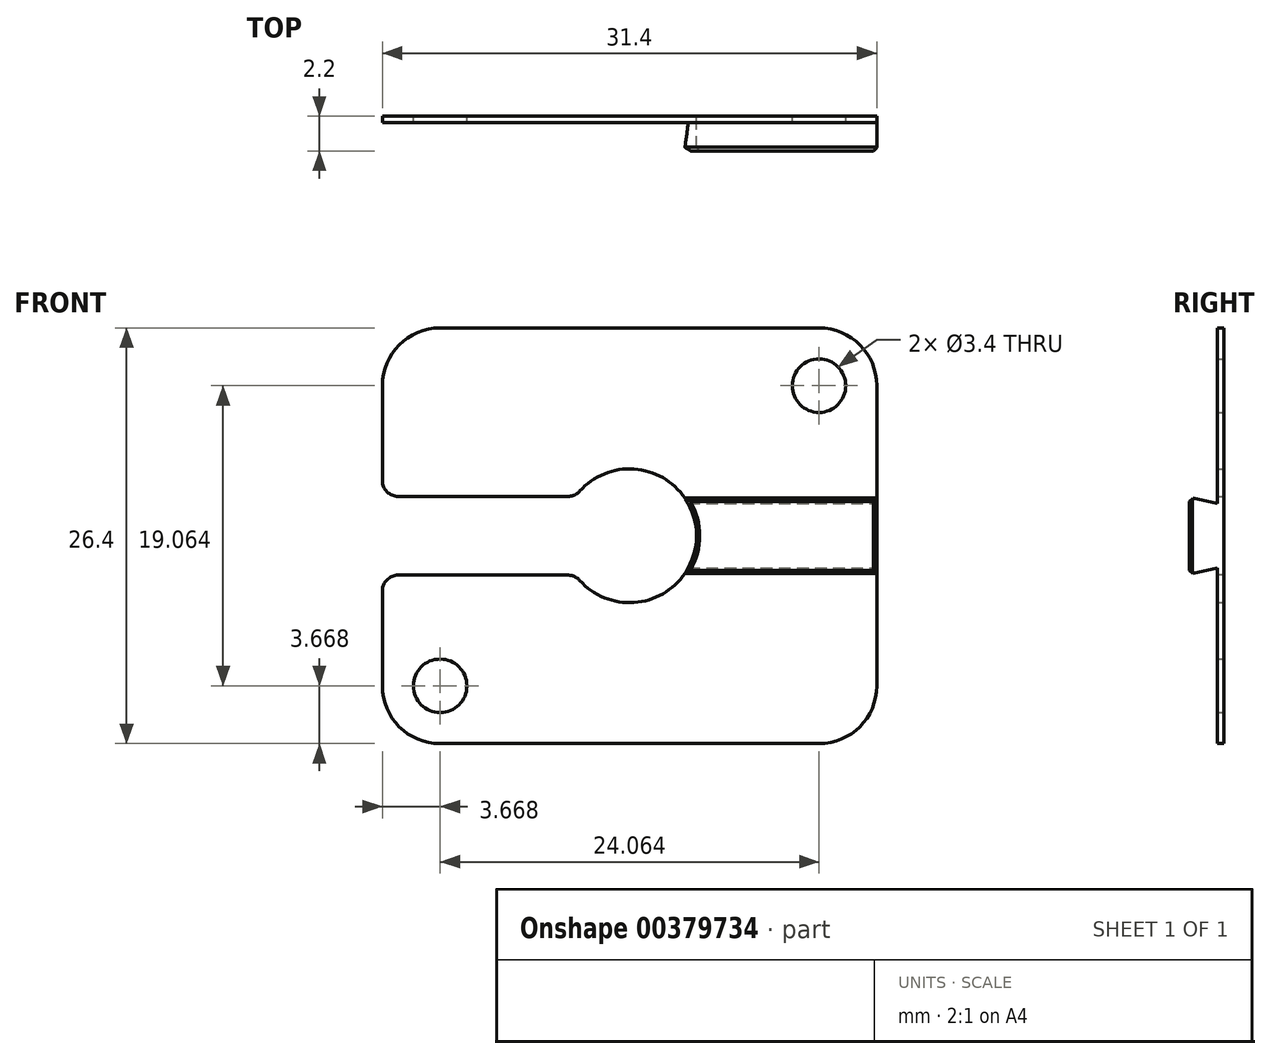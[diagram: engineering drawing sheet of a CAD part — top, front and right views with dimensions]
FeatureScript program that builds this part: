
annotation { "Feature Type Name" : "Feature", "Feature Type Description" : "" }
export const myFeature = defineFeature(function(context is Context, id is Id, definition is map)
    precondition{}
    {
        {
            var Q0;
            Q0=qCreatedBy(makeId("Front.planeOp"),FACE);
            var sketch = newSketch(context, id + "F0", { "sketchPlane" : qUnion([Q0])});
            skLineSegment(sketch, "E0.bottom", {"start": v(-15.7, 13.2) * mm, "end": v(15.7, 13.2) * mm});
            skLineSegment(sketch, "E0.top", {"start": v(-15.7, -13.2) * mm, "end": v(15.7, -13.2) * mm});
            skLineSegment(sketch, "E0.left", {"start": v(-15.7, 13.2) * mm, "end": v(-15.7, -13.2) * mm});
            skLineSegment(sketch, "E0.right", {"start": v(15.7, 13.2) * mm, "end": v(15.7, -13.2) * mm});
            skLineSegment(sketch, "E1.right", {"start": v(0, 0) * mm, "end": v(0, 13.2) * mm, "construction": true});
            skLineSegment(sketch, "E2.bottom", {"start": v(0, 0) * mm, "end": v(-15.7, 0) * mm, "construction": true});
            skLineSegment(sketch, "E2.top", {"start": v(0, 0) * mm, "end": v(-15.7, 0) * mm, "construction": true});
            skLineSegment(sketch, "E2.left", {"start": v(0, 0) * mm, "end": v(0, 0) * mm});
            skLineSegment(sketch, "E2.right", {"start": v(-15.7, 0) * mm, "end": v(-15.7, 0) * mm});
            skLineSegment(sketch, "E3", {"start": v(-12.03, 9.53) * mm, "end": v(12.03, -9.53) * mm, "construction": true});
            skCircle(sketch, "E4", {"center": v(-12.03, 9.53) * mm, "radius": 1.7 * mm, "construction": true});
            skCircle(sketch, "E5", {"center": v(12.03, -9.53) * mm, "radius": 1.7 * mm, "construction": true});
            skCircle(sketch, "E6", {"center": v(-12.03, 9.53) * mm, "radius": 3.67 * mm, "construction": true});
            skCircle(sketch, "E7", {"center": v(12.03, -9.53) * mm, "radius": 3.67 * mm, "construction": true});
            skCircle(sketch, "E8.MirrorC", {"center": v(12.03, 9.53) * mm, "radius": 1.7 * mm});
            skCircle(sketch, "E9.MirrorC", {"center": v(-12.03, -9.53) * mm, "radius": 1.7 * mm});
            skSolve(sketch);
        }
        {
            var Q0;
            Q0=qSketchRegion(id+"F0",true);
            extrude(context, id + "F1", {"entities" : qUnion([Q0]), "depth" : 0.4 * mm, "offsetDistance" : 25 * mm});
        }
        {
            var Q0;
            Q0=makeQuery(id+"F1.opExtrude","SWEPT_EDGE",EDGE,{"disambiguationData":[OSD([sQuery(id+"F0.wireOp",EDGE,"E0.top"),sQuery(id+"F0.wireOp",EDGE,"E0.right")])]});
            var Q1;
            Q1=makeQuery(id+"F1.opExtrude","SWEPT_EDGE",EDGE,{"disambiguationData":[OSD([sQuery(id+"F0.wireOp",EDGE,"E0.bottom"),sQuery(id+"F0.wireOp",EDGE,"E0.right")])]});
            var Q2;
            Q2=makeQuery(id+"F1.opExtrude","SWEPT_EDGE",EDGE,{"disambiguationData":[OSD([sQuery(id+"F0.wireOp",EDGE,"E0.top"),sQuery(id+"F0.wireOp",EDGE,"E0.left")])]});
            var Q3;
            Q3=makeQuery(id+"F1.opExtrude","SWEPT_EDGE",EDGE,{"disambiguationData":[OSD([sQuery(id+"F0.wireOp",EDGE,"E0.bottom"),sQuery(id+"F0.wireOp",EDGE,"E0.left")])]});
            fillet(context, id + "F2", {"entities" : qUnion([Q0, Q1, Q2, Q3]), "radius" : 3.66 * mm, "tangentPropagation" : true, "allowEdgeOverflow" : false});
        }
        {
            var Q0;
            Q0=qCreatedBy(makeId("Front.planeOp"),FACE);
            var sketch = newSketch(context, id + "F3", { "sketchPlane" : qUnion([Q0])});
            skArc(sketch, "E10", {"start": v(-3.44, -2.5) * mm, "mid": v(4.25, 0) * mm, "end": v(-3.44, 2.5) * mm});
            skLineSegment(sketch, "E11", {"start": v(-3.44, 2.5) * mm, "end": v(-21.94, 2.5) * mm});
            skLineSegment(sketch, "E12", {"start": v(-21.94, 2.5) * mm, "end": v(-21.94, -2.5) * mm});
            skLineSegment(sketch, "E13", {"start": v(-21.94, -2.5) * mm, "end": v(-3.44, -2.5) * mm});
            skLineSegment(sketch, "E14", {"start": v(0, 0) * mm, "end": v(-31.84, 0) * mm, "construction": true});
            skSolve(sketch);
        }
        {
            var Q0;
            Q0=qSketchRegion(id+"F3",true);
            extrude(context, id + "F4", {"entities" : qUnion([Q0]), "operationType" : NewBodyOperationType.REMOVE, "depth" : 25 * mm, "offsetDistance" : 25 * mm});
        }
        {
            var Q0;
            Q0=makeQuery(id+"F4.boolean.opBoolean","COPY",EDGE,{"derivedFrom":makeQuery(id+"F4.opExtrude","SWEPT_EDGE",EDGE,{"disambiguationData":[OSD([sQuery(id+"F3.wireOp",EDGE,"E10"),sQuery(id+"F3.wireOp",EDGE,"E13")])]})});
            var Q1;
            Q1=makeQuery(id+"F4.boolean.opBoolean","COPY",EDGE,{"derivedFrom":makeQuery(id+"F4.opExtrude","SWEPT_EDGE",EDGE,{"disambiguationData":[OSD([sQuery(id+"F3.wireOp",EDGE,"E10"),sQuery(id+"F3.wireOp",EDGE,"E11")])]})});
            var Q2;
            Q2=makeQuery(id+"F4.boolean.opBoolean","INTERSECT",EDGE,{"derivedFrom":[makeQuery(id+"F1.opExtrude","SWEPT_FACE",FACE,{"disambiguationData":[OSD([sQuery(id+"F0.wireOp",EDGE,"E0.left")])]}),makeQuery(id+"F4.opExtrude","SWEPT_FACE",FACE,{"disambiguationData":[OSD([sQuery(id+"F3.wireOp",EDGE,"E11")])]})]});
            var Q3;
            Q3=makeQuery(id+"F4.boolean.opBoolean","INTERSECT",EDGE,{"derivedFrom":[makeQuery(id+"F1.opExtrude","SWEPT_FACE",FACE,{"disambiguationData":[OSD([sQuery(id+"F0.wireOp",EDGE,"E0.left")])]}),makeQuery(id+"F4.opExtrude","SWEPT_FACE",FACE,{"disambiguationData":[OSD([sQuery(id+"F3.wireOp",EDGE,"E13")])]})]});
            fillet(context, id + "F5", {"entities" : qUnion([Q0, Q1, Q2, Q3]), "radius" : 1 * mm, "tangentPropagation" : true, "allowEdgeOverflow" : false});
        }
        {
            var Q0;
            Q0=makeQuery(id+"F1.opExtrude","CAP_FACE",FACE,{"disambiguationData":[OSD([sQuery(id+"F0.wireOp",EDGE,"E0.bottom"),sQuery(id+"F0.wireOp",EDGE,"E0.top"),sQuery(id+"F0.wireOp",EDGE,"E0.left"),sQuery(id+"F0.wireOp",EDGE,"E0.right"),sQuery(id+"F0.wireOp",EDGE,"E4"),sQuery(id+"F0.wireOp",EDGE,"E5")])],"isStart":true});
            var sketch = newSketch(context, id + "F6", { "sketchPlane" : qUnion([Q0])});
            skLineSegment(sketch, "E15", {"start": v(-15.7, 2.44) * mm, "end": v(-3.48, 2.44) * mm});
            skLineSegment(sketch, "E16", {"start": v(-15.7, -2.44) * mm, "end": v(-3.48, -2.44) * mm});
            skLineSegment(sketch, "E17", {"start": v(-17.91, 0) * mm, "end": v(0, 0) * mm, "construction": true});
            skPoint(sketch, "E17.startSnap0", {"position": v(-15.7, 0) * mm});
            skArc(sketch, "E18.0", {"start": v(-3.48, -2.44) * mm, "mid": v(-4.25, 0) * mm, "end": v(-3.48, 2.44) * mm});
            skLineSegment(sketch, "E19", {"start": v(-15.7, 2.44) * mm, "end": v(-15.7, -2.44) * mm});
            skPoint(sketch, "E20.orphan", {"position": v(3.17, 2.83) * mm});
            skPoint(sketch, "E21.orphan", {"position": v(3.17, -2.83) * mm});
            skSolve(sketch);
        }
        {
            var Q0;
            Q0 = qSketchRegion(id + "F6", true);
            extrude(context, id + "F7", {"entities" : qUnion([Q0]), "operationType" : NewBodyOperationType.ADD, "oppositeDirection" : true, "depth" : 2.2 * mm, "offsetDistance" : 25 * mm});
        }
        {
            var Q0;
            Q0=makeQuery(id+"F7.boolean.opBoolean","MERGE",FACE,{"derivedFrom":[makeQuery(id+"F1.opExtrude","SWEPT_FACE",FACE,{"disambiguationData":[OSD([sQuery(id+"F0.wireOp",EDGE,"E0.right")])]}),makeQuery(id+"F7.opExtrude","SWEPT_FACE",FACE,{"disambiguationData":[OSD([sQuery(id+"F6.wireOp",EDGE,"E19")])]})]});
            var sketch = newSketch(context, id + "F8", { "sketchPlane" : qUnion([Q0])});
            skLineSegment(sketch, "E22", {"start": v(-2.2, 2.44) * mm, "end": v(-0.4, 2.04) * mm});
            skLineSegment(sketch, "E23", {"start": v(-0.4, 2.04) * mm, "end": v(-0.4, 2.44) * mm});
            skLineSegment(sketch, "E24", {"start": v(-0.4, 2.44) * mm, "end": v(-2.2, 2.44) * mm});
            skLineSegment(sketch, "E25", {"start": v(-2.2, -2.44) * mm, "end": v(-0.4, -2.44) * mm});
            skLineSegment(sketch, "E26", {"start": v(-0.4, -2.44) * mm, "end": v(-0.4, -2.04) * mm});
            skLineSegment(sketch, "E27", {"start": v(-0.4, -2.04) * mm, "end": v(-2.2, -2.44) * mm});
            skLineSegment(sketch, "E28", {"start": v(0, 0) * mm, "end": v(-5.51, 0) * mm, "construction": true});
            skSolve(sketch);
        }
        {
            var Q0;
            Q0 = qSketchRegion(id + "F8", true);
            extrude(context, id + "F9", {"entities" : qUnion([Q0]), "operationType" : NewBodyOperationType.REMOVE, "oppositeDirection" : true, "depth" : 25 * mm, "offsetDistance" : 25 * mm});
        }
        {
            var Q0;
            Q0=makeQuery(id+"F7.opExtrude","CAP_FACE",FACE,{"disambiguationData":[OSD([sQuery(id+"F6.wireOp",EDGE,"E15"),sQuery(id+"F6.wireOp",EDGE,"E16"),sQuery(id+"F6.wireOp",EDGE,"E18.0"),sQuery(id+"F6.wireOp",EDGE,"E19")])],"isStart":false});
            chamfer(context, id + "F10", {"entities" : qUnion([Q0]), "width" : .2 * mm, "tangentPropagation" : true});
        }
    });
